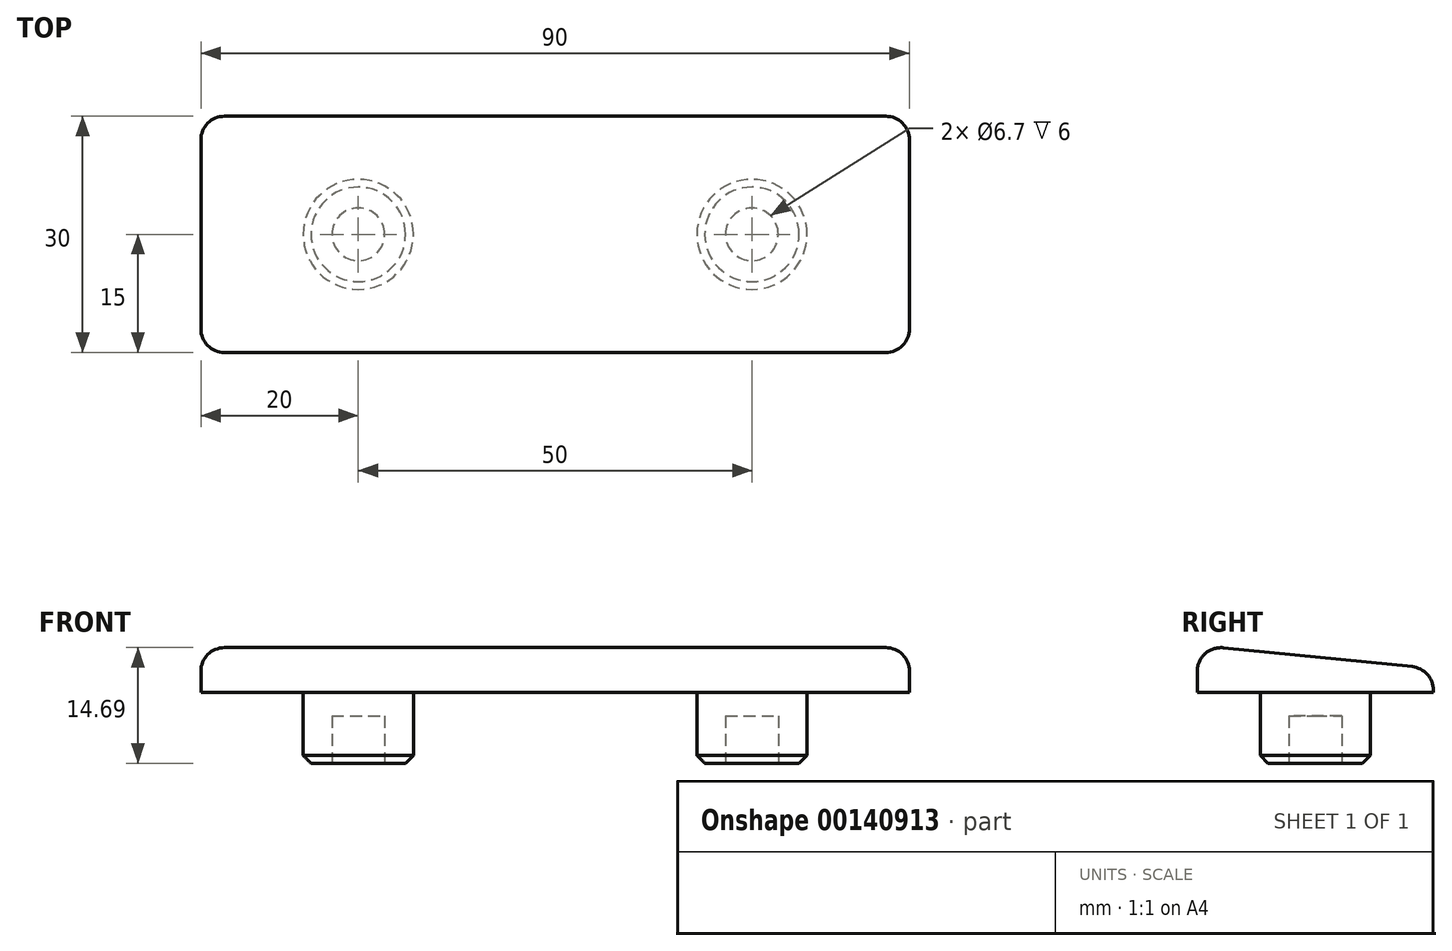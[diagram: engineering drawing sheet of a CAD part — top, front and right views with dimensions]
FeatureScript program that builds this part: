
annotation { "Feature Type Name" : "Feature", "Feature Type Description" : "" }
export const myFeature = defineFeature(function(context is Context, id is Id, definition is map)
    precondition{}
    {
        {
            var Q0;
            Q0=qCreatedBy(makeId("Right.planeOp"),FACE);
            var sketch = newSketch(context, id + "F0", { "sketchPlane" : qUnion([Q0])});
            skLineSegment(sketch, "E0", {"start": v(-15, 0) * mm, "end": v(-15, 6) * mm});
            skLineSegment(sketch, "E1", {"start": v(-15, 6) * mm, "end": v(15, 3) * mm});
            skLineSegment(sketch, "E2", {"start": v(15, 3) * mm, "end": v(15, 0) * mm});
            skLineSegment(sketch, "E3", {"start": v(15, 0) * mm, "end": v(-15, 0) * mm});
            skSolve(sketch);
        }
        {
            var Q0;
            Q0 = qSketchRegion(id + "F0", true);
            extrude(context, id + "F1", {"entities" : qUnion([Q0]), "depth" : 90 * mm});
        }
        {
            var Q0;
            Q0=qCreatedBy(makeId("Top.planeOp"),FACE);
            cPlane(context, id + "F2", {"entities" : qUnion([Q0]), "cplaneType" : CPlaneType.OFFSET, "offset" : 13 * mm, "width" : 150 * mm, "height" : 150 * mm});
        }
        {
            var Q0;
            Q0=makeQuery(id+"F1.opExtrude","SWEPT_FACE",FACE,{"disambiguationData":[OSD([sQuery(id+"F0.wireOp",EDGE,"E3")])]});
            var sketch = newSketch(context, id + "F3", { "sketchPlane" : qUnion([Q0])});
            skLineSegment(sketch, "E4", {"start": v(45, -30.01) * mm, "end": v(45, 30.01) * mm, "construction": true});
            skCircle(sketch, "E5", {"center": v(70, 0) * mm, "radius": 7 * mm});
            skCircle(sketch, "E6", {"center": v(20, 0) * mm, "radius": 7 * mm});
            skSolve(sketch);
        }
        {
            var Q0;
            Q0 = qSketchRegion(id + "F3", true);
            extrude(context, id + "F4", {"entities" : qUnion([Q0]), "operationType" : NewBodyOperationType.ADD, "depth" : 9 * mm});
        }
        {
            var Q0;
            Q0=makeQuery(id+"F4.opExtrude","CAP_FACE",FACE,{"disambiguationData":[OSD([sQuery(id+"F3.wireOp",EDGE,"E5")])],"isStart":false});
            var sketch = newSketch(context, id + "F5", { "sketchPlane" : qUnion([Q0])});
            skCircle(sketch, "E7", {"center": v(70, 0) * mm, "radius": 3.35 * mm});
            skCircle(sketch, "E8", {"center": v(20, 0) * mm, "radius": 3.35 * mm});
            skSolve(sketch);
        }
        {
            var Q0;
            Q0 = qSketchRegion(id + "F5", true);
            extrude(context, id + "F6", {"entities" : qUnion([Q0]), "operationType" : NewBodyOperationType.REMOVE, "oppositeDirection" : true, "depth" : 6 * mm});
        }
        {
            var Q0;
            Q0=makeQuery(id+"F4.opExtrude","CAP_EDGE",EDGE,{"disambiguationData":[OSD([sQuery(id+"F3.wireOp",EDGE,"E5")])],"isStart":false});
            var Q1;
            Q1=makeQuery(id+"F4.opExtrude","CAP_EDGE",EDGE,{"disambiguationData":[OSD([sQuery(id+"F3.wireOp",EDGE,"E6")])],"isStart":false});
            chamfer(context, id + "F7", {"entities" : qUnion([Q0, Q1]), "width" : 1 * mm, "tangentPropagation" : true});
        }
        {
            var Q0;
            Q0=makeQuery(id+"F1.opExtrude","CAP_EDGE",EDGE,{"disambiguationData":[OSD([sQuery(id+"F0.wireOp",EDGE,"E2")])],"isStart":false});
            var Q1;
            Q1=makeQuery(id+"F1.opExtrude","CAP_EDGE",EDGE,{"disambiguationData":[OSD([sQuery(id+"F0.wireOp",EDGE,"E2")])],"isStart":true});
            var Q2;
            Q2=makeQuery(id+"F1.opExtrude","CAP_EDGE",EDGE,{"disambiguationData":[OSD([sQuery(id+"F0.wireOp",EDGE,"E0")])],"isStart":true});
            var Q3;
            Q3=makeQuery(id+"F1.opExtrude","CAP_EDGE",EDGE,{"disambiguationData":[OSD([sQuery(id+"F0.wireOp",EDGE,"E0")])],"isStart":false});
            fillet(context, id + "F8", {"entities" : qUnion([Q0, Q1, Q2, Q3]), "radius" : 3 * mm, "tangentPropagation" : true, "allowEdgeOverflow" : false});
        }
        {
            var Q0;
            Q0=makeQuery(id+"F1.opExtrude","SWEPT_EDGE",EDGE,{"disambiguationData":[OSD([sQuery(id+"F0.wireOp",EDGE,"E1"),sQuery(id+"F0.wireOp",EDGE,"E2")])]});
            fillet(context, id + "F9", {"entities" : qUnion([Q0]), "radius" : 3 * mm, "tangentPropagation" : true, "allowEdgeOverflow" : false});
        }
    });
